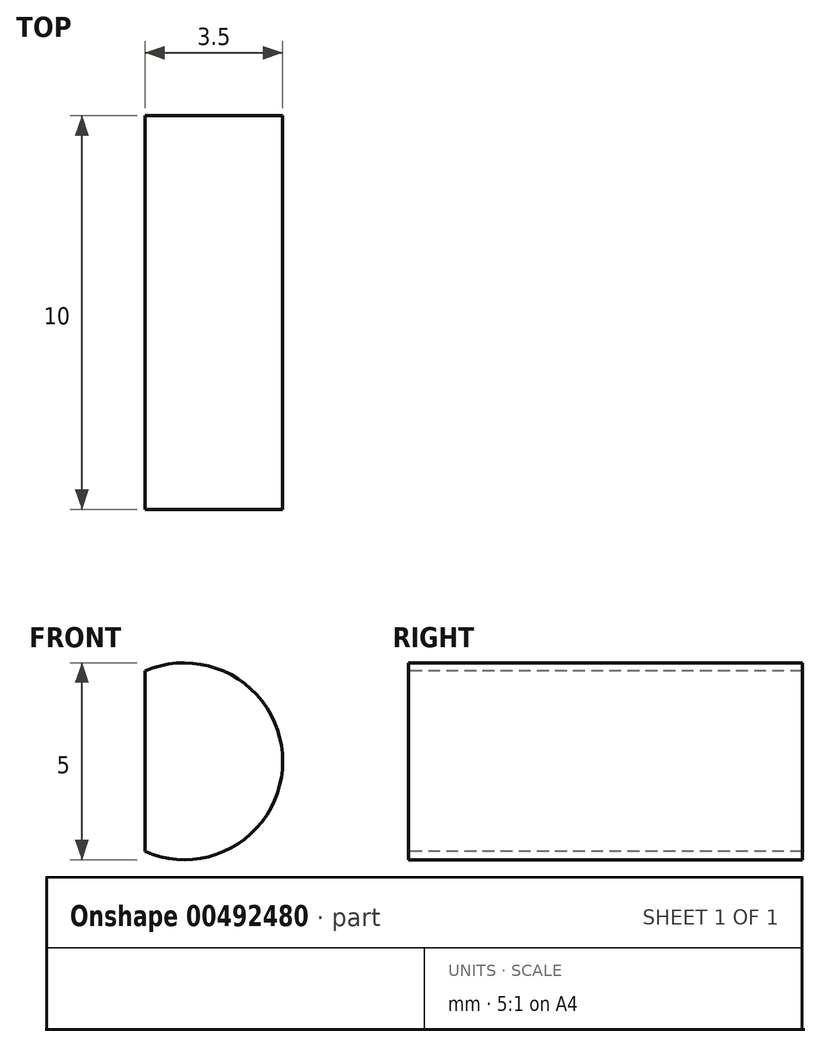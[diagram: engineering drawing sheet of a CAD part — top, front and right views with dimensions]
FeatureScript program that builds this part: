
annotation { "Feature Type Name" : "Feature", "Feature Type Description" : "" }
export const myFeature = defineFeature(function(context is Context, id is Id, definition is map)
    precondition{}
    {
        {
            var Q0;
            Q0=qCreatedBy(makeId("Front.planeOp"),FACE);
            var sketch = newSketch(context, id + "F0", { "sketchPlane" : qUnion([Q0])});
            skCircle(sketch, "E0", {"center": v(0, 0) * mm, "radius": 2.5 * mm});
            skSolve(sketch);
        }
        {
            var Q0;
            Q0=qSketchRegion(id+"F0",true);
            extrude(context, id + "F1", {"entities" : qUnion([Q0]), "depth" : 10 * mm});
        }
        {
            var Q0;
            Q0=makeQuery(id+"F1.opExtrude","CAP_FACE",FACE,{"disambiguationData":[OSD([sQuery(id+"F0.wireOp",EDGE,"E0")])],"isStart":false});
            var sketch = newSketch(context, id + "F2", { "sketchPlane" : qUnion([Q0])});
            skLineSegment(sketch, "E1", {"start": v(-1, 2.3) * mm, "end": v(-1, -2.3) * mm, "construction": true});
            skLineSegment(sketch, "E2.bottom", {"start": v(-1, 2.3) * mm, "end": v(-2.5, 2.3) * mm});
            skLineSegment(sketch, "E2.top", {"start": v(-1, -2.3) * mm, "end": v(-2.5, -2.3) * mm});
            skLineSegment(sketch, "E2.left", {"start": v(-1, 2.3) * mm, "end": v(-1, -2.3) * mm});
            skLineSegment(sketch, "E2.right", {"start": v(-2.5, 2.3) * mm, "end": v(-2.5, -2.3) * mm});
            skSolve(sketch);
        }
        {
            var Q0;
            Q0 = qSketchRegion(id + "F2", true);
            extrude(context, id + "F3", {"entities" : qUnion([Q0]), "operationType" : NewBodyOperationType.REMOVE, "endBound" : BoundingType.THROUGH_ALL, "oppositeDirection" : true, "depth" : 25 * mm});
        }
    });
